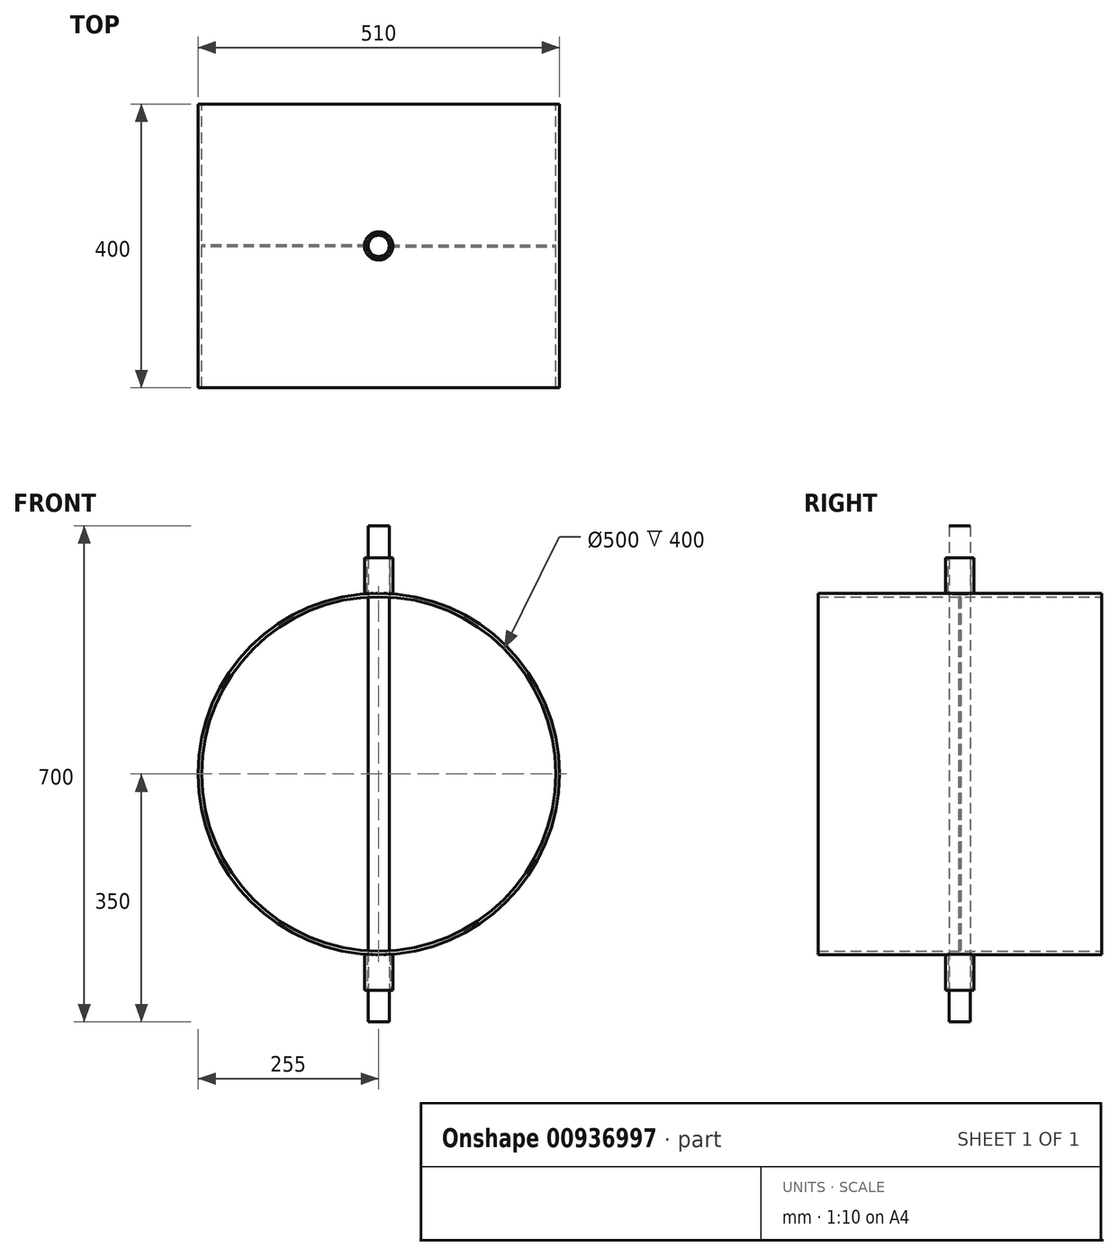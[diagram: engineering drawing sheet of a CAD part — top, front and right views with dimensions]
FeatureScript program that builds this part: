
annotation { "Feature Type Name" : "Feature", "Feature Type Description" : "" }
export const myFeature = defineFeature(function(context is Context, id is Id, definition is map)
    precondition{}
    {
        {
            var Q0;
            Q0=qCreatedBy(makeId("Front.planeOp"),FACE);
            var sketch = newSketch(context, id + "F0", { "sketchPlane" : qUnion([Q0])});
            skCircle(sketch, "E0", {"center": v(0, 0) * mm, "radius": 250 * mm});
            skLineSegment(sketch, "E1", {"start": v(-250, 0) * mm, "end": v(250, 0) * mm, "construction": true});
            skLineSegment(sketch, "E2", {"start": v(0, 250) * mm, "end": v(0, -250) * mm, "construction": true});
            skSolve(sketch);
        }
        {
            var Q0;
            Q0 = qSketchRegion(id + "F0", true);
            extrude(context, id + "F1", {"entities" : qUnion([Q0]), "endBound" : BoundingType.SYMMETRIC, "depth" : 2.5 * mm, "offsetDistance" : 25 * mm});
        }
        {
            var Q0;
            Q0=qCreatedBy(makeId("Top.planeOp"),FACE);
            var sketch = newSketch(context, id + "F2", { "sketchPlane" : qUnion([Q0])});
            skCircle(sketch, "E3", {"center": v(0, 0) * mm, "radius": 15 * mm});
            skSolve(sketch);
        }
        {
            var Q0;
            Q0 = qSketchRegion(id + "F2", true);
            extrude(context, id + "F3", {"entities" : qUnion([Q0]), "operationType" : NewBodyOperationType.ADD, "endBound" : BoundingType.SYMMETRIC, "depth" : 700 * mm, "offsetDistance" : 25 * mm});
        }
        {
            var Q0;
            Q0=qCreatedBy(makeId("Front.planeOp"),FACE);
            var sketch = newSketch(context, id + "F4", { "sketchPlane" : qUnion([Q0])});
            skCircle(sketch, "E4", {"center": v(0, 0) * mm, "radius": 250 * mm});
            skCircle(sketch, "E5.0", {"center": v(0, 0) * mm, "radius": 255 * mm});
            skSolve(sketch);
        }
        {
            var Q0;
            Q0 = qSketchRegion(id + "F4", true);
            extrude(context, id + "F5", {"entities" : qUnion([Q0]), "endBound" : BoundingType.SYMMETRIC, "depth" : 400 * mm, "offsetDistance" : 25 * mm});
        }
        {
            var Q0;
            Q0=qCreatedBy(makeId("Top.planeOp"),FACE);
            cPlane(context, id + "F6", {"entities" : qUnion([Q0]), "cplaneType" : CPlaneType.OFFSET, "offset" : 305 * mm, "width" : 150 * mm, "height" : 150 * mm});
        }
        {
            var Q0;
            Q0=qCreatedBy(id+"F6.planeOp",FACE);
            var sketch = newSketch(context, id + "F7", { "sketchPlane" : qUnion([Q0])});
            skCircle(sketch, "E6", {"center": v(0, 0) * mm, "radius": 20 * mm});
            skCircle(sketch, "E7", {"center": v(0, 0) * mm, "radius": 16 * mm});
            skSolve(sketch);
        }
        {
            var Q0;
            Q0 = qSketchRegion(id + "F7", true);
            extrude(context, id + "F8", {"entities" : qUnion([Q0]), "endBound" : BoundingType.UP_TO_NEXT, "oppositeDirection" : true, "depth" : 25 * mm, "offsetDistance" : 25 * mm});
        }
        {
            var Q0;
            Q0=makeQuery(id+"F8.opExtrude","SWEPT_BODY",BODY,{"disambiguationData":[OSD([sQuery(id+"F7.wireOp",EDGE,"E6"),sQuery(id+"F7.wireOp",EDGE,"E7")])]});
            var Q1;
            Q1=qCreatedBy(makeId("Top.planeOp"),FACE);
            mirror(context, id + "F9", {"entities" : qUnion([Q0]), "mirrorPlane" : qUnion([Q1])});
        }
        {
            var Q0;
            Q0=qCreatedBy(makeId("Top.planeOp"),FACE);
            cPlane(context, id + "F10", {"entities" : qUnion([Q0]), "cplaneType" : CPlaneType.OFFSET, "offset" : 305 * mm, "oppositeDirection" : true, "width" : 150 * mm, "height" : 150 * mm});
        }
    });
